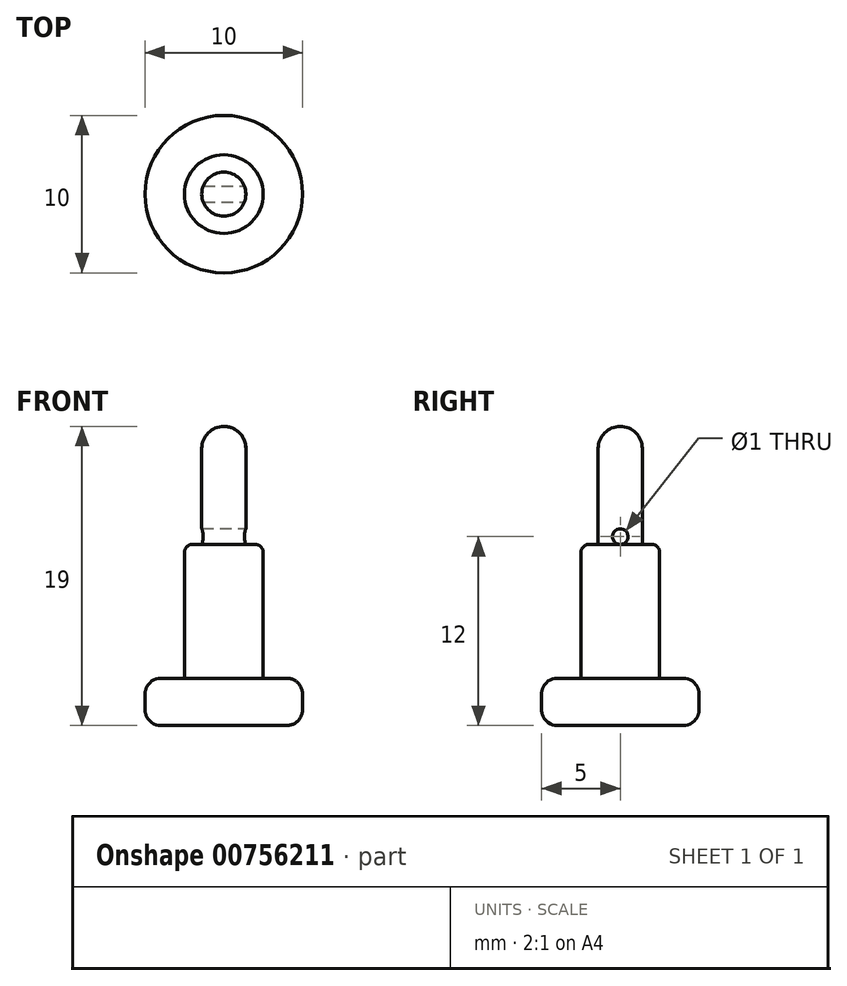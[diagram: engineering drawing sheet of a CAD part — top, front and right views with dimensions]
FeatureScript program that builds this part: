
annotation { "Feature Type Name" : "Feature", "Feature Type Description" : "" }
export const myFeature = defineFeature(function(context is Context, id is Id, definition is map)
    precondition{}
    {
        {
            var Q0;
            Q0=qCreatedBy(makeId("Top.planeOp"),FACE);
            var sketch = newSketch(context, id + "F0", { "sketchPlane" : qUnion([Q0])});
            skCircle(sketch, "E0", {"center": v(0, 0) * mm, "radius": 5 * mm});
            skSolve(sketch);
        }
        {
            var Q0;
            Q0=qSketchRegion(id+"F0",true);
            extrude(context, id + "F1", {"entities" : qUnion([Q0]), "depth" : 3 * mm, "offsetDistance" : 25 * mm});
        }
        {
            var Q0;
            Q0=makeQuery(id+"F1.opExtrude","CAP_FACE",FACE,{"disambiguationData":[OSD([sQuery(id+"F0.wireOp",EDGE,"E0")])],"isStart":false});
            var sketch = newSketch(context, id + "F2", { "sketchPlane" : qUnion([Q0])});
            skCircle(sketch, "E1", {"center": v(0, 0) * mm, "radius": 2.5 * mm});
            skSolve(sketch);
        }
        {
            var Q0;
            Q0=qSketchRegion(id+"F2",true);
            extrude(context, id + "F3", {"entities" : qUnion([Q0]), "operationType" : NewBodyOperationType.ADD, "depth" : 8.5 * mm, "offsetDistance" : 25 * mm});
        }
        {
            var Q0;
            Q0=makeQuery(id+"F3.opExtrude","CAP_FACE",FACE,{"disambiguationData":[OSD([sQuery(id+"F2.wireOp",EDGE,"E1")])],"isStart":false});
            var sketch = newSketch(context, id + "F4", { "sketchPlane" : qUnion([Q0])});
            skCircle(sketch, "E2", {"center": v(0, 0) * mm, "radius": 1.4 * mm});
            skSolve(sketch);
        }
        {
            var Q0;
            Q0=qSketchRegion(id+"F4",true);
            extrude(context, id + "F5", {"entities" : qUnion([Q0]), "operationType" : NewBodyOperationType.ADD, "depth" : 7.5 * mm, "offsetDistance" : 25 * mm});
        }
        {
            var Q0;
            Q0=makeQuery(id+"F5.opExtrude","CAP_FACE",FACE,{"disambiguationData":[OSD([sQuery(id+"F4.wireOp",EDGE,"E2")])],"isStart":false});
            fillet(context, id + "F6", {"entities" : qUnion([Q0]), "radius" : 1.4 * mm, "tangentPropagation" : true, "allowEdgeOverflow" : false});
        }
        {
            var Q0;
            Q0=makeQuery(id+"F3.opExtrude","CAP_EDGE",EDGE,{"disambiguationData":[OSD([sQuery(id+"F2.wireOp",EDGE,"E1")])],"isStart":true});
            var Q1;
            Q1=makeQuery(id+"F1.opExtrude","CAP_EDGE",EDGE,{"disambiguationData":[OSD([sQuery(id+"F0.wireOp",EDGE,"E0")])],"isStart":true});
            var Q2;
            Q2=makeQuery(id+"F1.opExtrude","CAP_EDGE",EDGE,{"disambiguationData":[OSD([sQuery(id+"F0.wireOp",EDGE,"E0")])],"isStart":false});
            fillet(context, id + "F7", {"entities" : qUnion([Q0, Q1, Q2]), "radius" : 1 * mm, "tangentPropagation" : true, "allowEdgeOverflow" : false});
        }
        {
            var Q0;
            Q0=makeQuery(id+"F5.opExtrude","CAP_EDGE",EDGE,{"disambiguationData":[OSD([sQuery(id+"F4.wireOp",EDGE,"E2")])],"isStart":true});
            var Q1;
            Q1=makeQuery(id+"F3.opExtrude","CAP_EDGE",EDGE,{"disambiguationData":[OSD([sQuery(id+"F2.wireOp",EDGE,"E1")])],"isStart":false});
            fillet(context, id + "F8", {"entities" : qUnion([Q0, Q1]), "radius" : .5 * mm, "tangentPropagation" : true, "allowEdgeOverflow" : false});
        }
        {
            var Q0;
            Q0=qCreatedBy(makeId("Right.planeOp"),FACE);
            var sketch = newSketch(context, id + "F9", { "sketchPlane" : qUnion([Q0])});
            skCircle(sketch, "E3", {"center": v(0, 12) * mm, "radius": 0.5 * mm});
            skLineSegment(sketch, "E4.0", {"start": v(-2.1, 11.5) * mm, "end": v(2, 11.5) * mm, "construction": true});
            skSolve(sketch);
        }
        {
            var Q0;
            Q0=qSketchRegion(id+"F9",true);
            extrude(context, id + "F10", {"entities" : qUnion([Q0]), "operationType" : NewBodyOperationType.REMOVE, "endBound" : BoundingType.SYMMETRIC, "oppositeDirection" : true, "depth" : 5 * mm, "offsetDistance" : 25 * mm});
        }
    });
